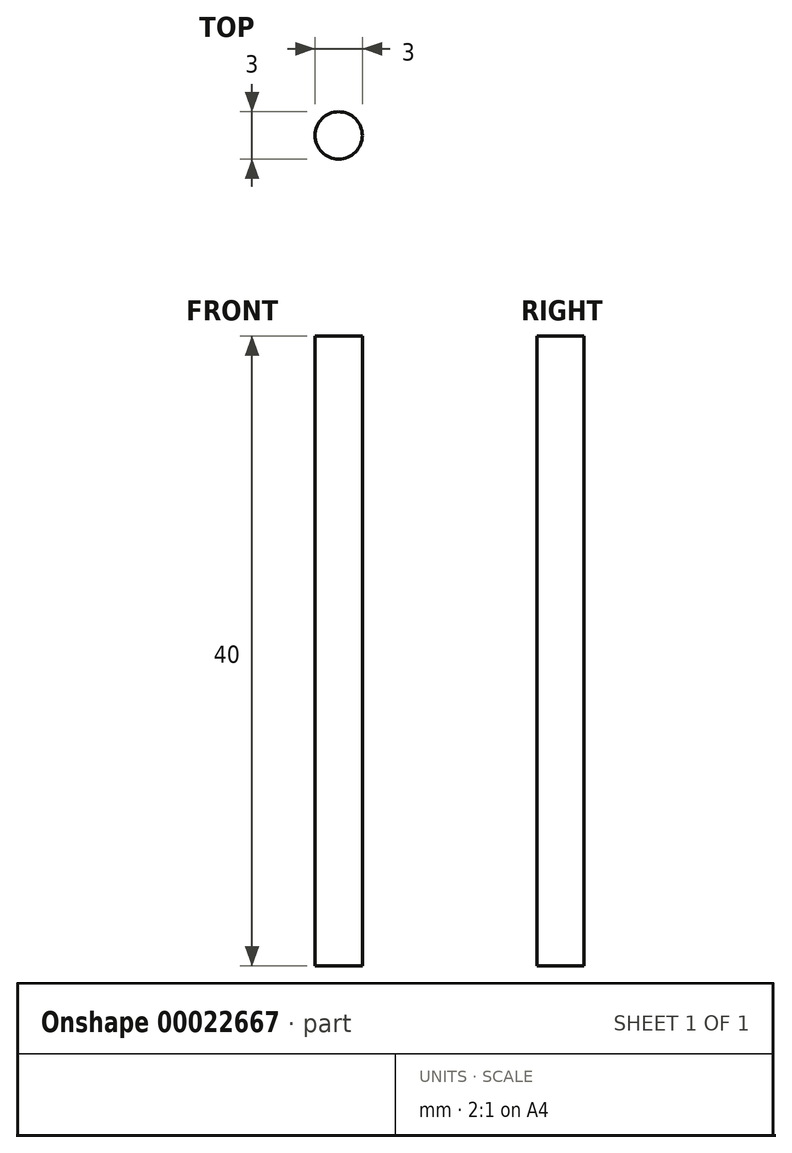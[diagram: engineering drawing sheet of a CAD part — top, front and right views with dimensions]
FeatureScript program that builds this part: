
annotation { "Feature Type Name" : "Feature", "Feature Type Description" : "" }
export const myFeature = defineFeature(function(context is Context, id is Id, definition is map)
    precondition{}
    {
        {
            var Q0;
            Q0=qCreatedBy(makeId("Top.planeOp"),FACE);
            var sketch = newSketch(context, id + "F0", { "sketchPlane" : qUnion([Q0])});
            skCircle(sketch, "E0", {"center": v(-13.7, 15.53) * mm, "radius": 1.5 * mm});
            skSolve(sketch);
        }
        {
            var Q0;
            Q0=makeQuery(id+"F0.imprint","IMPRINT",FACE,{"disambiguationData":[TD([[makeQuery(id+"F0.imprint","IMPRINT",EDGE,{"derivedFrom":sQuery(id+"F0.wireOp",EDGE,"E0")}),1.0]])]});
            extrude(context, id + "F1", {"entities" : qUnion([Q0]), "depth" : 40 * mm});
        }
    });
